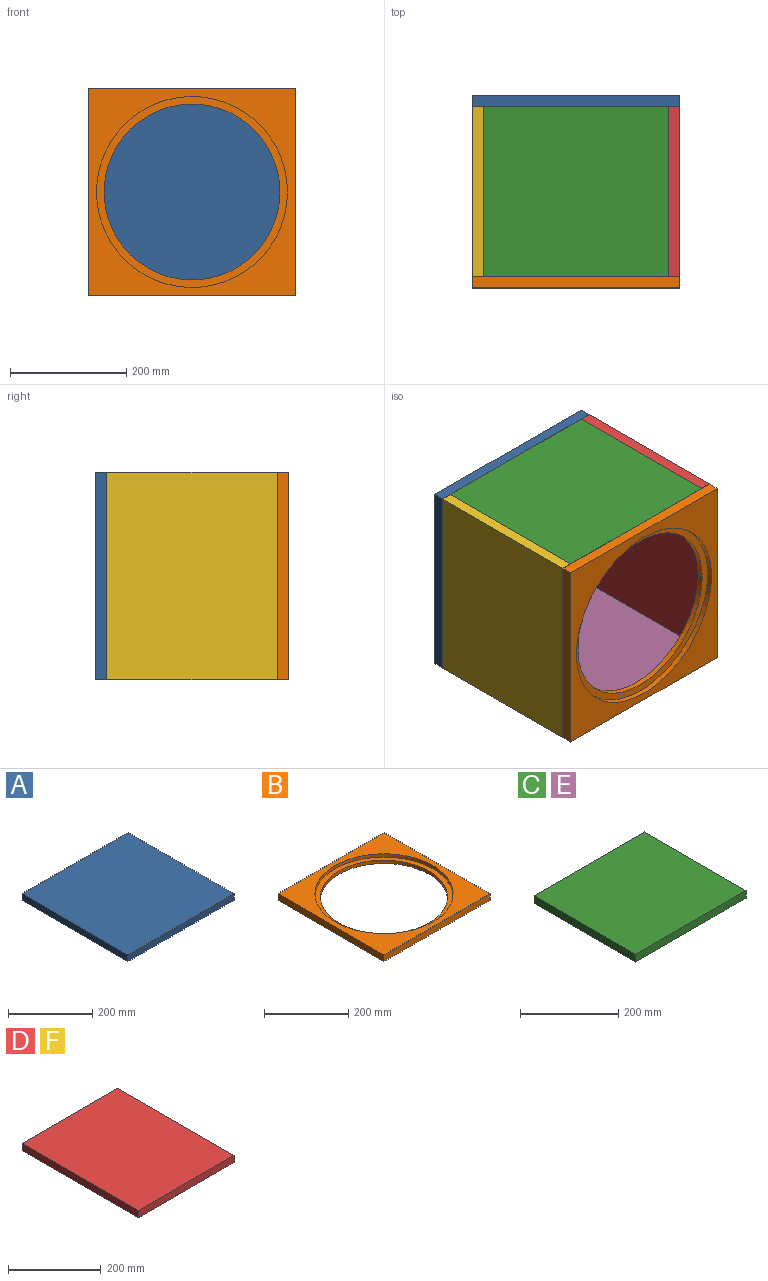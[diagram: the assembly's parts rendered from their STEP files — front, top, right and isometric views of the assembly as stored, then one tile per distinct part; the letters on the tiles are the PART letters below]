
ASSEMBLY  parts=6 mates=5
PART A: 6 faces, bbox 355.6x355.6x19 mm
  f0: plane 355.6x19mm, normal (0,1,0), area 6756.4mm2, adj f1,f3,f4,f5
  f1: plane 355.6x19mm, normal (-1,0,0), area 6756.4mm2, adj f0,f2,f4,f5
  f2: plane 355.6x19mm, normal (0,-1,0), area 6756.4mm2, adj f1,f3,f4,f5
  f3: plane 355.6x19mm, normal (1,0,0), area 6756.4mm2, adj f0,f2,f4,f5
  f4: plane 355.6x355.6mm, normal (0,0,1), area 126451.4mm2, adj f0,f1,f2,f3
  f5: plane 355.6x355.6mm, normal (0,0,-1), area 126451.4mm2, adj f0,f1,f2,f3
PART B: 9 faces, bbox 355.6x355.6x19 mm
  f0: plane 355.6x19mm, normal (0,1,0), area 6756.4mm2, adj f1,f4,f5,f6
  f1: plane 355.6x19mm, normal (-1,0,0), area 6756.4mm2, adj f0,f2,f5,f6
  f2: plane 355.6x19mm, normal (0,-1,0), area 6756.4mm2, adj f1,f4,f5,f6
  f3: cylinder r=164mm len=328mm, axis (0,0,-1), area 9789.2mm2, adj f5,f8
  f4: plane 355.6x19mm, normal (1,0,0), area 6756.4mm2, adj f0,f2,f5,f6
  f5: plane 355.6x355.6mm, normal (0,0,1), area 41955.1mm2, adj f0,f1,f2,f3,f4
  f6: plane 355.6x355.6mm, normal (0,0,-1), area 54819.9mm2, adj f0,f1,f2,f4,f7
  f7: cylinder r=151mm len=302mm, axis (0,0,-1), area 9013.2mm2, adj f6,f8
  f8: plane 328x328mm, normal (0,0,1), area 12864.8mm2, adj f3,f7
PART C: 6 faces, bbox 317.6x292.2x19 mm
  f0: plane 317.6x19mm, normal (0,1,0), area 6034.4mm2, adj f1,f3,f4,f5
  f1: plane 292.2x19mm, normal (-1,0,0), area 5551.8mm2, adj f0,f2,f4,f5
  f2: plane 317.6x19mm, normal (0,-1,0), area 6034.4mm2, adj f1,f3,f4,f5
  f3: plane 292.2x19mm, normal (1,0,0), area 5551.8mm2, adj f0,f2,f4,f5
  f4: plane 317.6x292.2mm, normal (0,0,1), area 92802.7mm2, adj f0,f1,f2,f3
  f5: plane 317.6x292.2mm, normal (0,0,-1), area 92802.7mm2, adj f0,f1,f2,f3
PART D: 6 faces, bbox 292.2x355.6x19 mm
  f0: plane 292.2x19mm, normal (0,1,0), area 5551.8mm2, adj f1,f3,f4,f5
  f1: plane 355.6x19mm, normal (-1,0,0), area 6756.4mm2, adj f0,f2,f4,f5
  f2: plane 292.2x19mm, normal (0,-1,0), area 5551.8mm2, adj f1,f3,f4,f5
  f3: plane 355.6x19mm, normal (1,0,0), area 6756.4mm2, adj f0,f2,f4,f5
  f4: plane 355.6x292.2mm, normal (0,0,1), area 103906.3mm2, adj f0,f1,f2,f3
  f5: plane 355.6x292.2mm, normal (0,0,-1), area 103906.3mm2, adj f0,f1,f2,f3
PART E: same geometry as C
PART F: same geometry as D
PLACE A rot(axis=(-1,0,0),90deg) t=(76.85,235.79,233.42)mm
PLACE B rot(axis=(1,0,0),90deg) t=(24.77,-56.41,183.01)mm
PLACE C t=(40.18,96.27,392.18)mm
PLACE D rot(axis=(0.58,0.58,0.58),120deg) t=(183.64,163.3,126.13)mm
PLACE E t=(40.18,96.27,55.58)mm
PLACE F rot(axis=(0.58,0.58,0.58),120deg) t=(-152.96,163.3,126.13)mm
MATE fastened F.f4 <-> E.f1  axis (1,0,0) through (-133.96,-56.41,55.58)mm
MATE fastened C.f3 <-> D.f5  axis (1,0,0) through (183.64,-56.41,411.18)mm
MATE fastened D.f5 <-> E.f3  axis (-1,0,0) through (183.64,235.79,55.58)mm
MATE fastened B.f6 <-> E.f2  axis (0,1,0) through (202.64,-56.41,55.58)mm
MATE fastened A.f5 <-> F.f3  axis (0,-1,0) through (-152.96,235.79,55.58)mm
